# Revit family: РВК_Муфта комбинированная разъемная раструбная ВР
name_source: partatom
category: Соединительные детали трубопроводов
revit_build: Autodesk Revit 2016 (Build: 20150714_1515(x64)
units: mm (PartAtom-declared; Revit-internal decimal feet)

## family parameters
Всегда вертикально = Да
На основе рабочей плоскости = Нет
Общий = Нет
При загрузке вырезать с полостями = Нет
Размер круглого соединителя = Использовать радиус
Тип детали = Соединение

## types (11) — shared parameters
ADSK_Завод-изготовитель = РВК
Материал стальной части = РВК_Сталь хромированная
Материал фитинга = РВК_Полипропилен PPR

## per-type parameters (varying)
| type | A | B | C | D | D+t | DN | G | GN | H | J | K | L1 | L2 | N | R | S1 | g |
| Муфта комбинированная разъемная раструбная D50-1 1/2'' ВР | 24 мм | 10 мм | 9 мм | 50 мм | 58 мм | 50 мм | 40 мм | 50 мм | 17 мм | 21 мм | 16 мм | 28 мм | 49 мм | 13 мм | 25 мм | 80 мм | 25 мм |
| Муфта комбинированная разъемная раструбная D40-1 1/4'' ВР | 21 мм | 15 мм | 7 мм | 40 мм | 48 мм | 40 мм | 32 мм | 40 мм | 13 мм | 17 мм | 12 мм | 31 мм | 50 мм | 12 мм | 20 мм | 63 мм | 20 мм |
| Муфта комбинированная разъемная раструбная D32-1 1/4'' ВР | 19 мм | 13 мм | 6 мм | 32 мм | 40 мм | 32 мм | 32 мм | 40 мм | 10 мм | 15 мм | 11 мм | 24 мм | 43 мм | 13 мм | 16 мм | 51 мм | 20 мм |
| Муфта комбинированная разъемная раструбная D32-1'' ВР | 19 мм | 13 мм | 6 мм | 32 мм | 40 мм | 32 мм | 25 мм | 32 мм | 10 мм | 15 мм | 11 мм | 24 мм | 40 мм | 9 мм | 16 мм | 51 мм | 16 мм |
| Муфта комбинированная разъемная раструбная D32-3/4'' ВР | 19 мм | 13 мм | 6 мм | 32 мм | 40 мм | 32 мм | 20 мм | 25 мм | 10 мм | 15 мм | 12 мм | 24 мм | 41 мм | 19 мм | 16 мм | 51 мм | 13 мм |
| Муфта комбинированная разъемная раструбная D25-1'' ВР | 17 мм | 13 мм | 6 мм | 25 мм | 33 мм | 25 мм | 25 мм | 32 мм | 12 мм | 15 мм | 12 мм | 24 мм | 43 мм | 13 мм | 13 мм | 45 мм | 16 мм |
| Муфта комбинированная разъемная раструбная D25-3/4'' ВР | 17 мм | 13 мм | 6 мм | 25 мм | 33 мм | 25 мм | 20 мм | 25 мм | 12 мм | 15 мм | 12 мм | 24 мм | 39 мм | 9 мм | 13 мм | 45 мм | 13 мм |
| Муфта комбинированная разъемная раструбная D25-1/2'' ВР | 17 мм | 13 мм | 6 мм | 25 мм | 33 мм | 25 мм | 15 мм | 20 мм | 12 мм | 15 мм | 9 мм | 24 мм | 38 мм | 8 мм | 13 мм | 45 мм | 10 мм |
| Муфта комбинированная разъемная раструбная D20-1'' ВР | 15 мм | 11 мм | 5 мм | 20 мм | 28 мм | 20 мм | 25 мм | 32 мм | 11 мм | 13 мм | 11 мм | 22 мм | 46 мм | 14 мм | 10 мм | 36 мм | 16 мм |
| Муфта комбинированная разъемная раструбная D20-3/4'' ВР | 15 мм | 11 мм | 5 мм | 20 мм | 28 мм | 20 мм | 20 мм | 25 мм | 11 мм | 13 мм | 9 мм | 22 мм | 36 мм | 6 мм | 10 мм | 36 мм | 13 мм |
| Муфта комбинированная разъемная раструбная D20-1/2'' ВР | 15 мм | 11 мм | 5 мм | 20 мм | 28 мм | 20 мм | 15 мм | 20 мм | 11 мм | 13 мм | 10 мм | 22 мм | 36 мм | 8 мм | 10 мм | 36 мм | 10 мм |

note: column(s) folded — value = type name in every type: Тип

## geometry (parser evidence)
native form markers: Blend x4
no freeform markers — native parametric forms only
